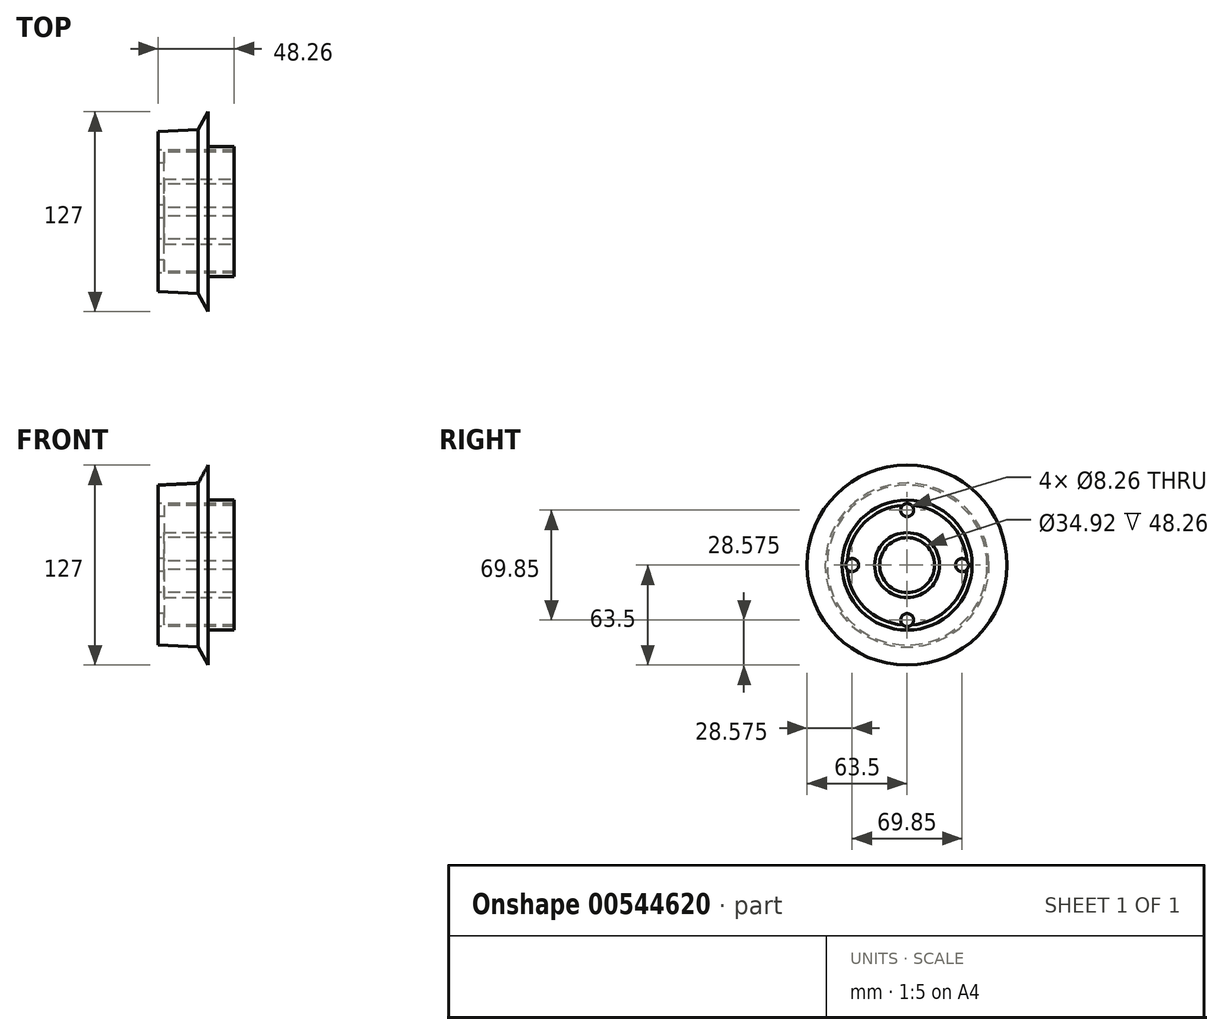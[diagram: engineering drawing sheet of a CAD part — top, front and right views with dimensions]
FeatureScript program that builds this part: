
annotation { "Feature Type Name" : "Feature", "Feature Type Description" : "" }
export const myFeature = defineFeature(function(context is Context, id is Id, definition is map)
    precondition{}
    {
        {
            var Q0;
            Q0=qCreatedBy(makeId("Front.planeOp"),FACE);
            var sketch = newSketch(context, id + "F0", { "sketchPlane" : qUnion([Q0])});
            skLineSegment(sketch, "E0", {"start": v(0, 17.46) * mm, "end": v(0, 50.8) * mm});
            skLineSegment(sketch, "E1", {"start": v(0, 50.8) * mm, "end": v(25.4, 52.07) * mm});
            skLineSegment(sketch, "E2", {"start": v(25.4, 52.07) * mm, "end": v(31.75, 63.5) * mm});
            skLineSegment(sketch, "E3", {"start": v(31.75, 63.5) * mm, "end": v(31.75, 41.28) * mm});
            skLineSegment(sketch, "E4", {"start": v(31.75, 41.28) * mm, "end": v(48.26, 41.28) * mm});
            skLineSegment(sketch, "E5", {"start": v(48.26, 41.28) * mm, "end": v(48.26, 17.46) * mm});
            skLineSegment(sketch, "E6", {"start": v(0, 17.46) * mm, "end": v(48.26, 17.46) * mm});
            skLineSegment(sketch, "E7", {"start": v(0, 0) * mm, "end": v(83.39, 0) * mm, "construction": true});
            skSolve(sketch);
        }
        {
            var Q0;
            Q0=makeQuery(id+"F0.imprint","IMPRINT",FACE,{"disambiguationData":[TD([[makeQuery(id+"F0.imprint","IMPRINT",EDGE,{"derivedFrom":sQuery(id+"F0.wireOp",EDGE,"E0")}),-1.0]])]});
            var Q1;
            Q1=sQuery(id+"F0.wireOp",EDGE,"E7");
            revolve(context, id + "F1", {"surfaceOperationType" : NewSurfaceOperationType.NEW, "entities" : qUnion([Q0]), "axis" : qUnion([Q1]), "revolveType" : RevolveType.FULL});
        }
        {
            var Q0;
            Q0=makeQuery(id+"F1.opRevolve","SWEPT_FACE",FACE,{"disambiguationData":[OSD([sQuery(id+"F0.wireOp",EDGE,"E5")])]});
            var sketch = newSketch(context, id + "F2", { "sketchPlane" : qUnion([Q0])});
            skCircle(sketch, "E8", {"center": v(0, 0) * mm, "radius": 38.1 * mm});
            skCircle(sketch, "E9", {"center": v(0, 0) * mm, "radius": 20.65 * mm});
            skSolve(sketch);
        }
        {
            var Q0;
            Q0=makeQuery(id+"F2.imprint","IMPRINT",FACE,{"disambiguationData":[TD([[makeQuery(id+"F2.imprint","IMPRINT",EDGE,{"derivedFrom":sQuery(id+"F2.wireOp",EDGE,"E8")}),1.0]])]});
            extrude(context, id + "F3", {"entities" : qUnion([Q0]), "operationType" : NewBodyOperationType.REMOVE, "oppositeDirection" : true, "depth" : 44.45 * mm, "offsetDistance" : 25.4 * mm});
        }
        {
            var Q0;
            Q0=qCreatedBy(makeId("Right.planeOp"),FACE);
            var sketch = newSketch(context, id + "F4", { "sketchPlane" : qUnion([Q0])});
            skCircle(sketch, "E10", {"center": v(0, 0) * mm, "radius": 34.92 * mm, "construction": true});
            skPoint(sketch, "E11", {"position": v(34.93, 0) * mm});
            skPoint(sketch, "E12", {"position": v(0, 34.93) * mm});
            skPoint(sketch, "E13", {"position": v(-34.93, 0) * mm});
            skPoint(sketch, "E14", {"position": v(0, -34.93) * mm});
            skLineSegment(sketch, "E15", {"start": v(0, 0) * mm, "end": v(34.93, 0) * mm, "construction": true});
            skLineSegment(sketch, "E16", {"start": v(0, -34.93) * mm, "end": v(0, 0) * mm, "construction": true});
            skLineSegment(sketch, "E17", {"start": v(-34.93, 0) * mm, "end": v(0, 0) * mm, "construction": true});
            skLineSegment(sketch, "E18", {"start": v(0, 34.92) * mm, "end": v(0, 0) * mm, "construction": true});
            skSolve(sketch);
        }
        {
            var Q0;
            Q0=sQuery(id+"F4.wireOp",VERTEX,"E13");
            var Q1;
            Q1=sQuery(id+"F4.wireOp",VERTEX,"E16.start");
            var Q2;
            Q2=sQuery(id+"F4.wireOp",VERTEX,"E11");
            var Q3;
            Q3=sQuery(id+"F4.wireOp",VERTEX,"E12");
            var Q4;
            Q4=makeQuery(id+"F1.opRevolve","SWEPT_BODY",BODY,{"disambiguationData":[OSD([sQuery(id+"F0.wireOp",EDGE,"E0"),sQuery(id+"F0.wireOp",EDGE,"E1"),sQuery(id+"F0.wireOp",EDGE,"E2"),sQuery(id+"F0.wireOp",EDGE,"E3"),sQuery(id+"F0.wireOp",EDGE,"E4"),sQuery(id+"F0.wireOp",EDGE,"E5"),sQuery(id+"F0.wireOp",EDGE,"E6")])]});
            hole(context, id + "F5", {"style" : HoleStyle.SIMPLE, "endStyle" : HoleEndStyle.THROUGH, "oppositeDirection" : true, "holeDiameter" : 8.25 * mm, "majorDiameter" : 6.35 * mm, "isTappedThrough" : true, "tappedDepth" : 12.7 * mm, "tapClearance" : 3, "locations" : qUnion([Q0, Q1, Q2, Q3]), "scope" : qUnion([Q4])});
        }
    });
